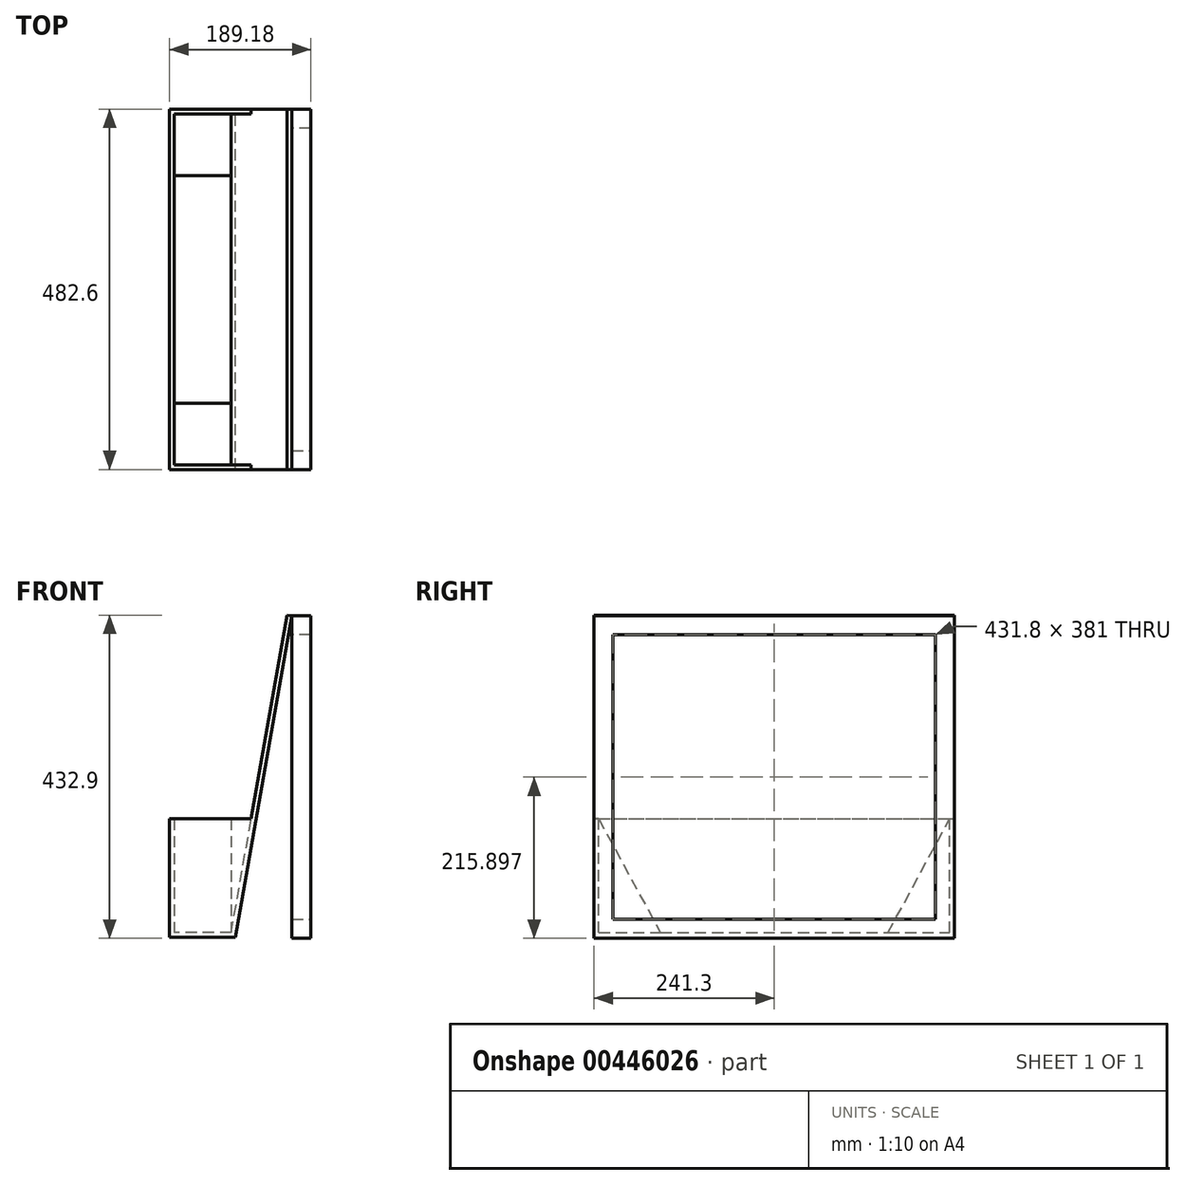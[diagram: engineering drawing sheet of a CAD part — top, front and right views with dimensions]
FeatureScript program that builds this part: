
annotation { "Feature Type Name" : "Feature", "Feature Type Description" : "" }
export const myFeature = defineFeature(function(context is Context, id is Id, definition is map)
    precondition{}
    {
        {
            var Q0;
            Q0=qCreatedBy(makeId("Front.planeOp"),FACE);
            var sketch = newSketch(context, id + "F0", { "sketchPlane" : qUnion([Q0])});
            skLineSegment(sketch, "E0", {"start": v(0, 0) * mm, "end": v(76.2, 0) * mm});
            skLineSegment(sketch, "E1", {"start": v(76.2, 0) * mm, "end": v(151.18, 425.24) * mm});
            skLineSegment(sketch, "E2", {"start": v(0, 0) * mm, "end": v(0, 152.4) * mm});
            skLineSegment(sketch, "E3", {"start": v(151.18, 425.24) * mm, "end": v(157.43, 424.14) * mm});
            skLineSegment(sketch, "E4", {"start": v(0, 0) * mm, "end": v(0, -6.35) * mm});
            skLineSegment(sketch, "E5", {"start": v(157.43, 424.14) * mm, "end": v(81.53, -6.35) * mm});
            skLineSegment(sketch, "E6", {"start": v(0, -6.35) * mm, "end": v(81.53, -6.35) * mm});
            skLineSegment(sketch, "E7", {"start": v(0, -6.35) * mm, "end": v(-6.35, -6.35) * mm});
            skLineSegment(sketch, "E8", {"start": v(-6.35, -6.35) * mm, "end": v(-6.35, 0) * mm});
            skLineSegment(sketch, "E9", {"start": v(-6.35, 0) * mm, "end": v(-6.35, 152.4) * mm});
            skLineSegment(sketch, "E10", {"start": v(-6.35, 152.4) * mm, "end": v(0, 152.4) * mm});
            skSolve(sketch);
        }
        {
            var Q0;
            Q0 = qSketchRegion(id + "F0", true);
            extrude(context, id + "F1", {"entities" : qUnion([Q0]), "depth" : 482.6 * mm});
        }
        {
            var Q0;
            Q0=makeQuery(id+"F1.opExtrude","SWEPT_FACE",FACE,{"disambiguationData":[OSD([sQuery(id+"F0.wireOp",EDGE,"E2")])]});
            var sketch = newSketch(context, id + "F2", { "sketchPlane" : qUnion([Q0])});
            skLineSegment(sketch, "E11", {"start": v(0, 0) * mm, "end": v(0, 152.4) * mm});
            skLineSegment(sketch, "E12", {"start": v(0, 152.4) * mm, "end": v(-6.35, 152.4) * mm});
            skLineSegment(sketch, "E13", {"start": v(-6.35, 152.4) * mm, "end": v(-6.35, 0) * mm});
            skLineSegment(sketch, "E14", {"start": v(-6.35, 0) * mm, "end": v(0, 0) * mm});
            skSolve(sketch);
        }
        {
            var Q0;
            Q0 = qSketchRegion(id + "F2", true);
            extrude(context, id + "F3", {"entities" : qUnion([Q0]), "operationType" : NewBodyOperationType.ADD, "depth" : 76.2 * mm});
        }
        {
            var Q0;
            Q0=makeQuery(id+"F1.opExtrude","SWEPT_FACE",FACE,{"disambiguationData":[OSD([sQuery(id+"F0.wireOp",EDGE,"E2")])]});
            var sketch = newSketch(context, id + "F4", { "sketchPlane" : qUnion([Q0])});
            skLineSegment(sketch, "E15", {"start": v(-482.6, 0) * mm, "end": v(-482.6, 152.4) * mm});
            skLineSegment(sketch, "E16", {"start": v(-482.6, 152.4) * mm, "end": v(-476.25, 152.4) * mm});
            skLineSegment(sketch, "E17", {"start": v(-476.25, 152.4) * mm, "end": v(-476.25, 0) * mm});
            skLineSegment(sketch, "E18", {"start": v(-476.25, 0) * mm, "end": v(-482.6, 0) * mm});
            skSolve(sketch);
        }
        {
            var Q0;
            Q0 = qSketchRegion(id + "F4", true);
            extrude(context, id + "F5", {"entities" : qUnion([Q0]), "operationType" : NewBodyOperationType.ADD, "depth" : 76.2 * mm});
        }
        {
            var Q0;
            Q0=makeQuery(id+"F3.boolean.opBoolean","MERGE",FACE,{"derivedFrom":[makeQuery(id+"F1.opExtrude","CAP_FACE",FACE,{"disambiguationData":[OSD([sQuery(id+"F0.wireOp",EDGE,"E0"),sQuery(id+"F0.wireOp",EDGE,"E1"),sQuery(id+"F0.wireOp",EDGE,"E2"),sQuery(id+"F0.wireOp",EDGE,"E3"),sQuery(id+"F0.wireOp",EDGE,"E5"),sQuery(id+"F0.wireOp",EDGE,"E6"),sQuery(id+"F0.wireOp",EDGE,"E7"),sQuery(id+"F0.wireOp",EDGE,"E8"),sQuery(id+"F0.wireOp",EDGE,"E9"),sQuery(id+"F0.wireOp",EDGE,"E10")])],"isStart":true}),makeQuery(id+"F3.opExtrude","SWEPT_FACE",FACE,{"disambiguationData":[OSD([sQuery(id+"F2.wireOp",EDGE,"E11")])]})]});
            var sketch = newSketch(context, id + "F6", { "sketchPlane" : qUnion([Q0])});
            skLineSegment(sketch, "E19", {"start": v(-76.2, 152.4) * mm, "end": v(-103.07, 152.4) * mm});
            skLineSegment(sketch, "E20", {"start": v(-103.07, 152.4) * mm, "end": v(-76.2, 0) * mm});
            skLineSegment(sketch, "E21", {"start": v(-76.2, 0) * mm, "end": v(-76.2, 152.4) * mm});
            skSolve(sketch);
        }
        {
            var Q0;
            Q0 = qSketchRegion(id + "F6", true);
            extrude(context, id + "F7", {"entities" : qUnion([Q0]), "operationType" : NewBodyOperationType.ADD, "oppositeDirection" : true, "depth" : 6.35 * mm});
        }
        {
            var Q0;
            Q0=makeQuery(id+"F5.boolean.opBoolean","MERGE",FACE,{"derivedFrom":[makeQuery(id+"F1.opExtrude","CAP_FACE",FACE,{"disambiguationData":[OSD([sQuery(id+"F0.wireOp",EDGE,"E0"),sQuery(id+"F0.wireOp",EDGE,"E1"),sQuery(id+"F0.wireOp",EDGE,"E2"),sQuery(id+"F0.wireOp",EDGE,"E3"),sQuery(id+"F0.wireOp",EDGE,"E5"),sQuery(id+"F0.wireOp",EDGE,"E6"),sQuery(id+"F0.wireOp",EDGE,"E7"),sQuery(id+"F0.wireOp",EDGE,"E8"),sQuery(id+"F0.wireOp",EDGE,"E9"),sQuery(id+"F0.wireOp",EDGE,"E10")])],"isStart":false}),makeQuery(id+"F5.opExtrude","SWEPT_FACE",FACE,{"disambiguationData":[OSD([sQuery(id+"F4.wireOp",EDGE,"E15")])]})]});
            var sketch = newSketch(context, id + "F8", { "sketchPlane" : qUnion([Q0])});
            skLineSegment(sketch, "E22", {"start": v(76.2, 152.4) * mm, "end": v(103.07, 152.4) * mm});
            skLineSegment(sketch, "E23", {"start": v(103.07, 152.4) * mm, "end": v(76.2, 0) * mm});
            skLineSegment(sketch, "E24", {"start": v(76.2, 0) * mm, "end": v(76.2, 152.4) * mm});
            skSolve(sketch);
        }
        {
            var Q0;
            Q0 = qSketchRegion(id + "F8", true);
            extrude(context, id + "F9", {"entities" : qUnion([Q0]), "operationType" : NewBodyOperationType.ADD, "oppositeDirection" : true, "depth" : 6.35 * mm});
        }
        {
            var Q0;
            Q0=makeQuery(id+"F1.opExtrude","SWEPT_FACE",FACE,{"disambiguationData":[OSD([sQuery(id+"F0.wireOp",EDGE,"E2")])]});
            var sketch = newSketch(context, id + "F10", { "sketchPlane" : qUnion([Q0])});
            skLineSegment(sketch, "E25", {"start": v(-88.9, 0) * mm, "end": v(-6.35, 152.4) * mm});
            skLineSegment(sketch, "E26", {"start": v(-6.35, 152.4) * mm, "end": v(-6.35, 0) * mm});
            skLineSegment(sketch, "E27", {"start": v(-6.35, 0) * mm, "end": v(-88.9, 0) * mm});
            skSolve(sketch);
        }
        {
            var Q0;
            Q0 = qSketchRegion(id + "F10", true);
            extrude(context, id + "F11", {"entities" : qUnion([Q0]), "operationType" : NewBodyOperationType.ADD, "depth" : 76.2 * mm});
        }
        {
            var Q0;
            Q0=makeQuery(id+"F1.opExtrude","SWEPT_FACE",FACE,{"disambiguationData":[OSD([sQuery(id+"F0.wireOp",EDGE,"E2")])]});
            var sketch = newSketch(context, id + "F12", { "sketchPlane" : qUnion([Q0])});
            skLineSegment(sketch, "E28", {"start": v(-476.25, 0) * mm, "end": v(-476.25, 152.4) * mm});
            skLineSegment(sketch, "E29", {"start": v(-476.25, 152.4) * mm, "end": v(-393.7, 0) * mm});
            skLineSegment(sketch, "E30", {"start": v(-393.7, 0) * mm, "end": v(-476.25, 0) * mm});
            skSolve(sketch);
        }
        {
            var Q0;
            Q0 = qSketchRegion(id + "F12", true);
            extrude(context, id + "F13", {"entities" : qUnion([Q0]), "operationType" : NewBodyOperationType.ADD, "depth" : 76.2 * mm});
        }
        {
            var Q0;
            Q0=makeQuery(id+"F7.boolean.opBoolean","MERGE",FACE,{"derivedFrom":[makeQuery(id+"F3.boolean.opBoolean","MERGE",FACE,{"derivedFrom":[makeQuery(id+"F1.opExtrude","CAP_FACE",FACE,{"disambiguationData":[OSD([sQuery(id+"F0.wireOp",EDGE,"E0"),sQuery(id+"F0.wireOp",EDGE,"E1"),sQuery(id+"F0.wireOp",EDGE,"E2"),sQuery(id+"F0.wireOp",EDGE,"E3"),sQuery(id+"F0.wireOp",EDGE,"E5"),sQuery(id+"F0.wireOp",EDGE,"E6"),sQuery(id+"F0.wireOp",EDGE,"E7"),sQuery(id+"F0.wireOp",EDGE,"E8"),sQuery(id+"F0.wireOp",EDGE,"E9"),sQuery(id+"F0.wireOp",EDGE,"E10")])],"isStart":true}),makeQuery(id+"F3.opExtrude","SWEPT_FACE",FACE,{"disambiguationData":[OSD([sQuery(id+"F2.wireOp",EDGE,"E11")])]})]}),makeQuery(id+"F7.opExtrude","CAP_FACE",FACE,{"disambiguationData":[OSD([sQuery(id+"F6.wireOp",EDGE,"E19"),sQuery(id+"F6.wireOp",EDGE,"E20"),sQuery(id+"F6.wireOp",EDGE,"E21")])],"isStart":true})]});
            var sketch = newSketch(context, id + "F14", { "sketchPlane" : qUnion([Q0])});
            skLineSegment(sketch, "E31", {"start": v(-157.43, 424.14) * mm, "end": v(-182.83, 424.14) * mm});
            skLineSegment(sketch, "E32", {"start": v(-182.83, 424.14) * mm, "end": v(-182.83, -7.66) * mm});
            skLineSegment(sketch, "E33", {"start": v(-182.83, -7.66) * mm, "end": v(-157.43, -7.66) * mm});
            skLineSegment(sketch, "E34", {"start": v(-157.43, -7.66) * mm, "end": v(-157.43, 424.14) * mm});
            skSolve(sketch);
        }
        {
            var Q0;
            Q0 = qSketchRegion(id + "F14", true);
            extrude(context, id + "F15", {"entities" : qUnion([Q0]), "oppositeDirection" : true, "depth" : 25.4 * mm});
        }
        {
            var Q0;
            Q0=makeQuery(id+"F15.opExtrude","CAP_FACE",FACE,{"disambiguationData":[OSD([sQuery(id+"F14.wireOp",EDGE,"E31"),sQuery(id+"F14.wireOp",EDGE,"E32"),sQuery(id+"F14.wireOp",EDGE,"E33"),sQuery(id+"F14.wireOp",EDGE,"E34")])],"isStart":false});
            var sketch = newSketch(context, id + "F16", { "sketchPlane" : qUnion([Q0])});
            skLineSegment(sketch, "E35", {"start": v(157.43, -7.66) * mm, "end": v(157.43, 17.74) * mm});
            skLineSegment(sketch, "E36", {"start": v(157.43, 17.74) * mm, "end": v(182.83, 17.74) * mm});
            skLineSegment(sketch, "E37", {"start": v(182.83, 17.74) * mm, "end": v(182.83, -7.66) * mm});
            skLineSegment(sketch, "E38", {"start": v(182.83, -7.66) * mm, "end": v(157.43, -7.66) * mm});
            skLineSegment(sketch, "E39", {"start": v(182.83, 424.14) * mm, "end": v(182.83, 398.74) * mm});
            skLineSegment(sketch, "E40", {"start": v(182.83, 398.74) * mm, "end": v(157.43, 398.74) * mm});
            skLineSegment(sketch, "E41", {"start": v(157.43, 398.74) * mm, "end": v(157.43, 424.14) * mm});
            skLineSegment(sketch, "E42", {"start": v(157.43, 424.14) * mm, "end": v(182.83, 424.14) * mm});
            skSolve(sketch);
        }
        {
            var Q0;
            Q0 = qSketchRegion(id + "F16", true);
            extrude(context, id + "F17", {"entities" : qUnion([Q0]), "operationType" : NewBodyOperationType.ADD, "depth" : 431.8 * mm});
        }
        {
            var Q0;
            Q0=makeQuery(id+"F17.opExtrude","CAP_FACE",FACE,{"disambiguationData":[OSD([sQuery(id+"F16.wireOp",EDGE,"E39"),sQuery(id+"F16.wireOp",EDGE,"E40"),sQuery(id+"F16.wireOp",EDGE,"E41"),sQuery(id+"F16.wireOp",EDGE,"E42")])],"isStart":false});
            var sketch = newSketch(context, id + "F18", { "sketchPlane" : qUnion([Q0])});
            skLineSegment(sketch, "E43", {"start": v(182.83, 424.14) * mm, "end": v(182.83, -7.66) * mm});
            skLineSegment(sketch, "E44", {"start": v(182.83, -7.66) * mm, "end": v(157.43, -7.66) * mm});
            skLineSegment(sketch, "E45", {"start": v(157.43, -7.66) * mm, "end": v(157.43, 424.14) * mm});
            skLineSegment(sketch, "E46", {"start": v(157.43, 424.14) * mm, "end": v(182.83, 424.14) * mm});
            skSolve(sketch);
        }
        {
            var Q0;
            Q0 = qSketchRegion(id + "F18", true);
            extrude(context, id + "F19", {"entities" : qUnion([Q0]), "operationType" : NewBodyOperationType.ADD, "depth" : 25.4 * mm});
        }
    });
